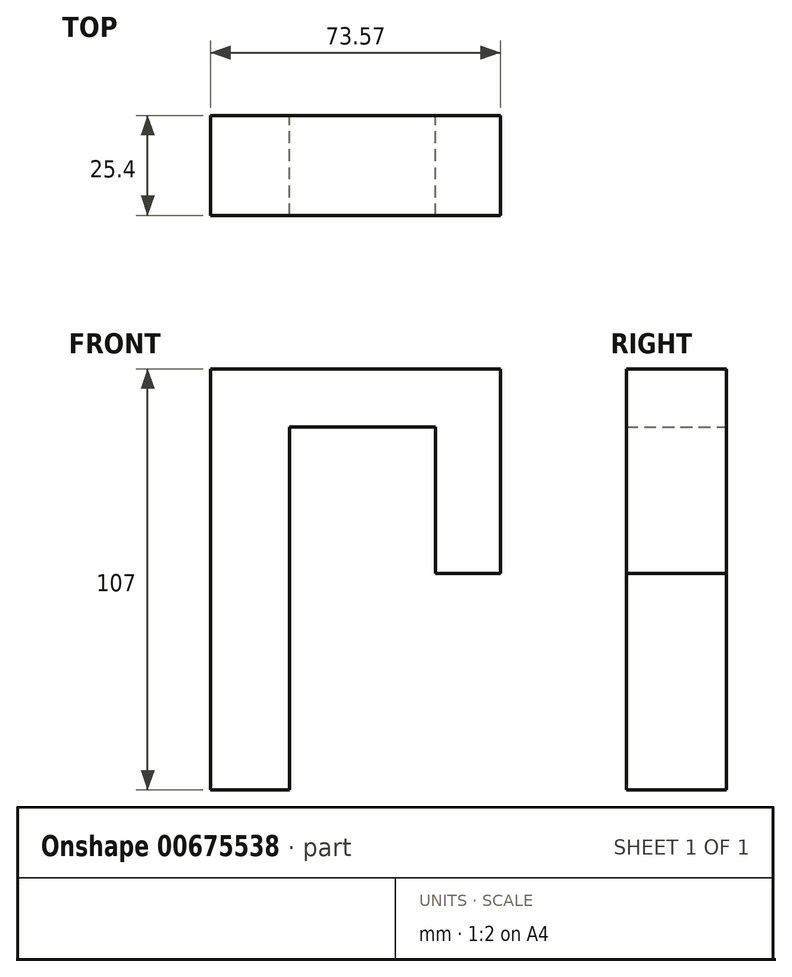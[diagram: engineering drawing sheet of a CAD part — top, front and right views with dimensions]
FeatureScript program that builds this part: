
annotation { "Feature Type Name" : "Feature", "Feature Type Description" : "" }
export const myFeature = defineFeature(function(context is Context, id is Id, definition is map)
    precondition{}
    {
        {
            var Q0;
            Q0=qCreatedBy(makeId("Front.planeOp"),FACE);
            var sketch = newSketch(context, id + "F0", { "sketchPlane" : qUnion([Q0])});
            skLineSegment(sketch, "E0", {"start": v(-123.72, 51.94) * mm, "end": v(-123.72, -55.06) * mm});
            skLineSegment(sketch, "E1", {"start": v(-123.72, 51.94) * mm, "end": v(-50.15, 51.94) * mm});
            skLineSegment(sketch, "E2", {"start": v(-50.15, 51.94) * mm, "end": v(-50.15, 0) * mm});
            skLineSegment(sketch, "E3", {"start": v(-50.15, 0) * mm, "end": v(-66.65, 0) * mm});
            skLineSegment(sketch, "E4", {"start": v(-66.65, 0) * mm, "end": v(-66.65, 37.23) * mm});
            skLineSegment(sketch, "E5", {"start": v(-66.65, 37.23) * mm, "end": v(-103.65, 37.23) * mm});
            skLineSegment(sketch, "E6", {"start": v(-103.65, 37.23) * mm, "end": v(-103.65, -55.06) * mm});
            skLineSegment(sketch, "E7", {"start": v(-103.65, -55.06) * mm, "end": v(-123.72, -55.06) * mm});
            skSolve(sketch);
        }
        {
            var Q0;
            Q0 = qSketchRegion(id + "F0", true);
            extrude(context, id + "F1", {"entities" : qUnion([Q0]), "depth" : 25.4 * mm, "offsetDistance" : 25.4 * mm});
        }
    });
